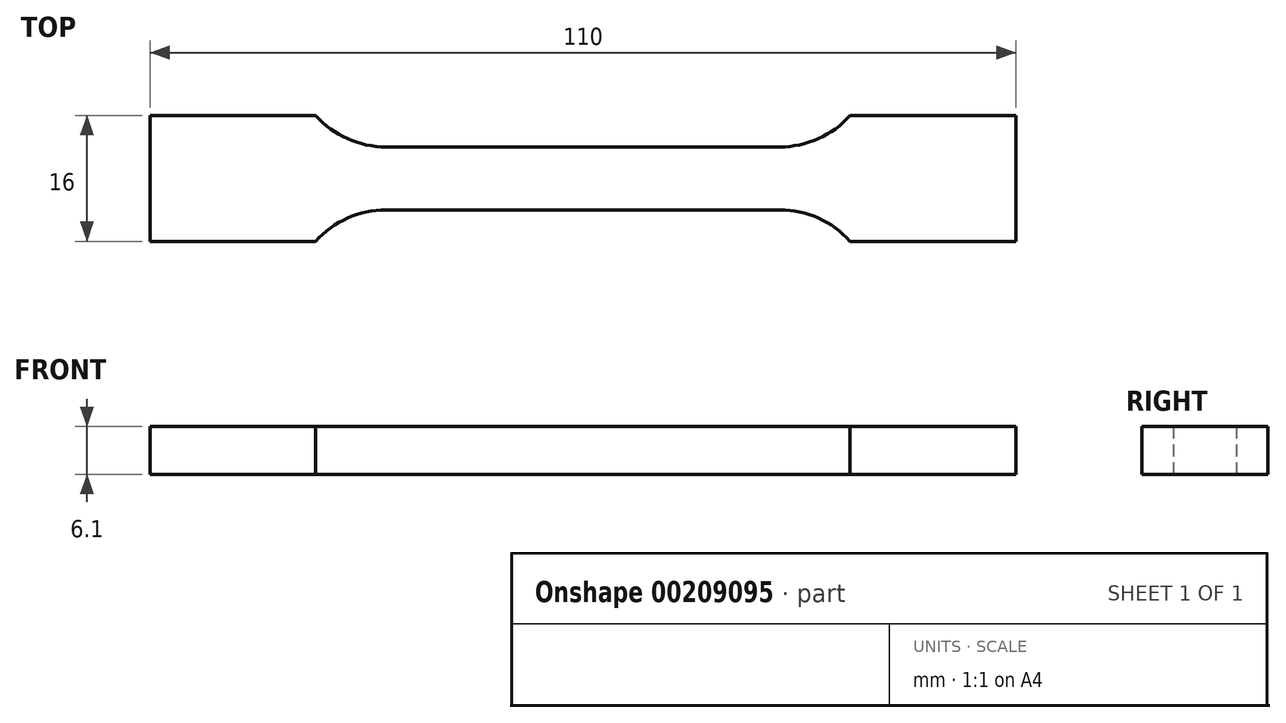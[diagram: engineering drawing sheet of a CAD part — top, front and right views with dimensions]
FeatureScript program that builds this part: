
annotation { "Feature Type Name" : "Feature", "Feature Type Description" : "" }
export const myFeature = defineFeature(function(context is Context, id is Id, definition is map)
    precondition{}
    {
        {
            var Q0;
            Q0=qCreatedBy(makeId("Top.planeOp"),FACE);
            var sketch = newSketch(context, id + "F0", { "sketchPlane" : qUnion([Q0])});
            skLineSegment(sketch, "E0.bottom", {"start": v(25, -4) * mm, "end": v(-25, -4) * mm});
            skLineSegment(sketch, "E0.top", {"start": v(25, 4) * mm, "end": v(-25, 4) * mm});
            skPoint(sketch, "E0.middle", {"position": v(0, 0) * mm});
            skLineSegment(sketch, "E1.bottom", {"start": v(55, -8) * mm, "end": v(33.94, -8) * mm});
            skLineSegment(sketch, "E1.top", {"start": v(55, 8) * mm, "end": v(33.94, 8) * mm});
            skLineSegment(sketch, "E1.left", {"start": v(55, -8) * mm, "end": v(55, 8) * mm});
            skPoint(sketch, "E1.middle", {"position": v(44.47, 0) * mm});
            skLineSegment(sketch, "E2.bottom", {"start": v(-33.94, 8) * mm, "end": v(-55, 8) * mm});
            skLineSegment(sketch, "E2.top", {"start": v(-33.94, -8) * mm, "end": v(-55, -8) * mm});
            skLineSegment(sketch, "E2.right", {"start": v(-55, 8) * mm, "end": v(-55, -8) * mm});
            skPoint(sketch, "E2.middle", {"position": v(-44.47, 0) * mm});
            skArc(sketch, "E3", {"start": v(-25, 4) * mm, "mid": v(-29.9, 5.05) * mm, "end": v(-33.94, 8) * mm});
            skArc(sketch, "E4", {"start": v(-25, -4) * mm, "mid": v(-29.9, -5.05) * mm, "end": v(-33.94, -8) * mm});
            skArc(sketch, "E5", {"start": v(25, 4) * mm, "mid": v(29.9, 5.05) * mm, "end": v(33.94, 8) * mm});
            skArc(sketch, "E6", {"start": v(25, -4) * mm, "mid": v(29.9, -5.05) * mm, "end": v(33.94, -8) * mm});
            skSolve(sketch);
        }
        {
            var Q0;
            Q0=makeQuery(id+"F0.imprint","IMPRINT",FACE,{"disambiguationData":[TD([[makeQuery(id+"F0.imprint","IMPRINT",EDGE,{"derivedFrom":sQuery(id+"F0.wireOp",EDGE,"E0.bottom")}),-1.0]])]});
            extrude(context, id + "F1", {"entities" : qUnion([Q0]), "depth" : 6.1 * mm, "symmetric" : true});
        }
    });
